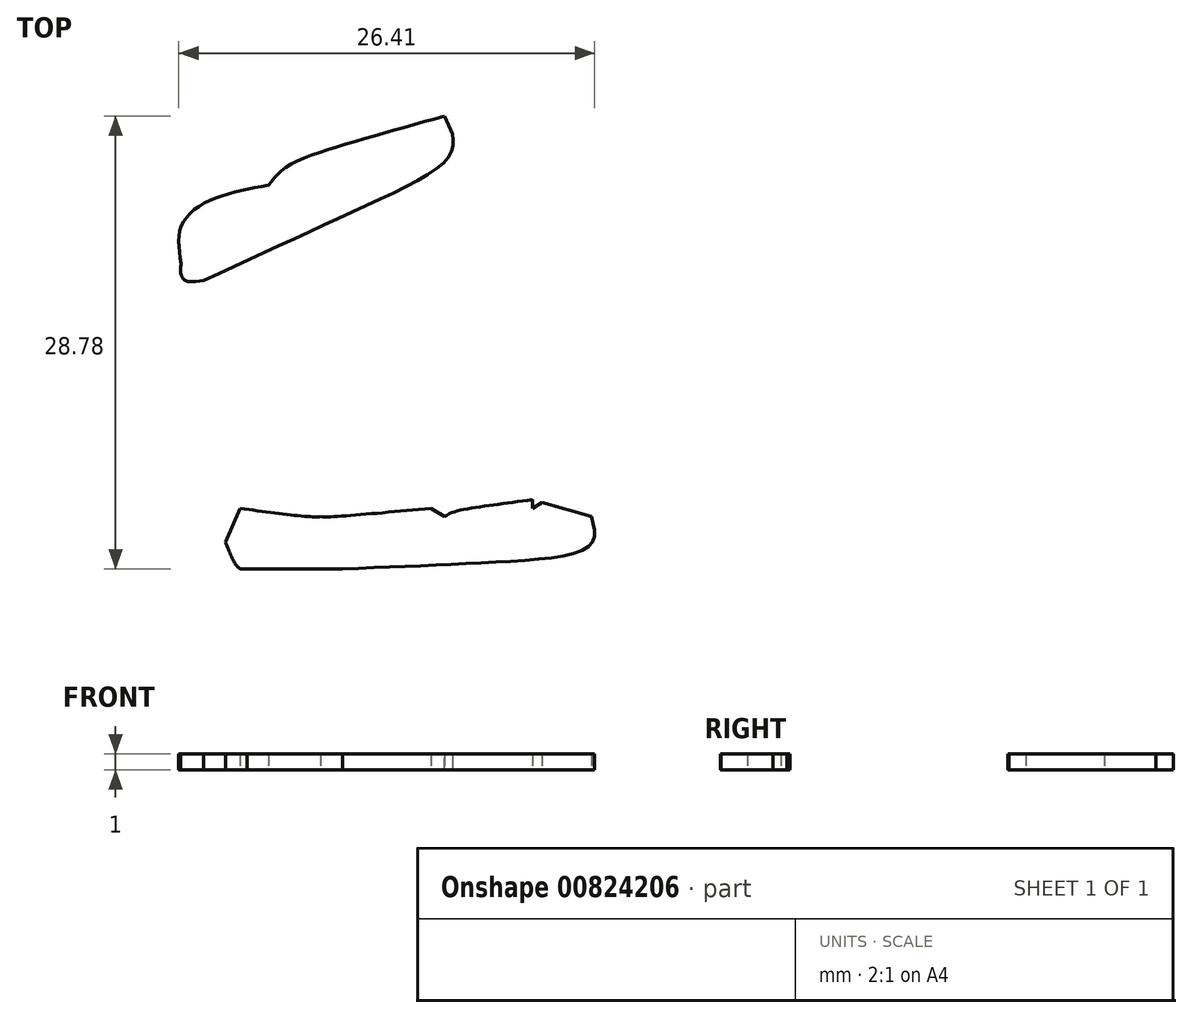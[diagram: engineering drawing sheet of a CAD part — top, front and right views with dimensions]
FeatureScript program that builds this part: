
annotation { "Feature Type Name" : "Feature", "Feature Type Description" : "" }
export const myFeature = defineFeature(function(context is Context, id is Id, definition is map)
    precondition{}
    {
        {
            var Q0;
            Q0=qCreatedBy(makeId("Top.planeOp"),FACE);
            var sketch = newSketch(context, id + "F0", { "sketchPlane" : qUnion([Q0])});
            skLineSegment(sketch, "E0", {"start": v(-130.54, 32.73) * mm, "end": v(-129.62, 32.73) * mm});
            skLineSegment(sketch, "E1", {"start": v(-129.62, 32.73) * mm, "end": v(-130.54, 32.73) * mm});
            skLineSegment(sketch, "E2", {"start": v(-121.63, 45.27) * mm, "end": v(-120.16, 45.27) * mm});
            skLineSegment(sketch, "E3", {"start": v(-120.16, 45.27) * mm, "end": v(-121.63, 45.27) * mm});
            skLineSegment(sketch, "E4", {"start": v(-119.52, 44.51) * mm, "end": v(-119.52, 36.1) * mm});
            skLineSegment(sketch, "E5", {"start": v(-119.52, 36.1) * mm, "end": v(-119.52, 44.51) * mm});
            skLineSegment(sketch, "E6", {"start": v(-112.28, 38.7) * mm, "end": v(-111.49, 37.23) * mm});
            skLineSegment(sketch, "E7", {"start": v(-111.49, 37.23) * mm, "end": v(-111.49, 36.47) * mm});
            skLineSegment(sketch, "E8", {"start": v(-111.49, 36.47) * mm, "end": v(-112.28, 38.7) * mm});
            skLineSegment(sketch, "E9", {"start": v(-129.26, 16.37) * mm, "end": v(-129.26, 17.5) * mm});
            skLineSegment(sketch, "E10", {"start": v(-129.26, 17.5) * mm, "end": v(-129.26, 16.37) * mm});
            skLineSegment(sketch, "E11", {"start": v(-131.13, 17.5) * mm, "end": v(-132.17, 17.5) * mm});
            skLineSegment(sketch, "E12", {"start": v(-132.17, 17.5) * mm, "end": v(-131.13, 17.5) * mm});
            skLineSegment(sketch, "E13", {"start": v(-133.76, 19.58) * mm, "end": v(-133.76, 26.11) * mm});
            skLineSegment(sketch, "E14", {"start": v(-133.76, 26.11) * mm, "end": v(-134.47, 27.77) * mm});
            skLineSegment(sketch, "E15", {"start": v(-134.47, 27.77) * mm, "end": v(-133.76, 19.58) * mm});
            skLineSegment(sketch, "E16", {"start": v(-144.82, 25.3) * mm, "end": v(-144.82, 26.58) * mm});
            skLineSegment(sketch, "E17", {"start": v(-144.82, 26.58) * mm, "end": v(-144.82, 25.3) * mm});
            skLineSegment(sketch, "E18", {"start": v(-134.32, 31.6) * mm, "end": v(-133.76, 34.91) * mm});
            skLineSegment(sketch, "E19", {"start": v(-133.76, 34.91) * mm, "end": v(-134.32, 31.6) * mm});
            skLineSegment(sketch, "E20", {"start": v(-135.79, 44.56) * mm, "end": v(-135.79, 45.27) * mm});
            skLineSegment(sketch, "E21", {"start": v(-135.79, 45.27) * mm, "end": v(-135.79, 44.56) * mm});
            skLineSegment(sketch, "E22", {"start": v(-141.2, 19.58) * mm, "end": v(-140.2, 19.58) * mm});
            skLineSegment(sketch, "E23", {"start": v(-140.2, 19.58) * mm, "end": v(-141.2, 19.58) * mm});
            skLineSegment(sketch, "E24", {"start": v(-115.06, 17.17) * mm, "end": v(-112.6, 17.17) * mm});
            skLineSegment(sketch, "E25", {"start": v(-112.6, 17.17) * mm, "end": v(-115.06, 17.17) * mm});
            skLineSegment(sketch, "E26", {"start": v(-108.46, 12.3) * mm, "end": v(-108.46, 11.21) * mm});
            skLineSegment(sketch, "E27", {"start": v(-108.46, 11.21) * mm, "end": v(-108.46, 12.3) * mm});
            skLineSegment(sketch, "E28", {"start": v(-125.53, -19.25) * mm, "end": v(-124.53, -19.25) * mm});
            skLineSegment(sketch, "E29", {"start": v(-124.53, -19.25) * mm, "end": v(-125.53, -19.25) * mm});
            skLineSegment(sketch, "E30", {"start": v(-89.89, -19.96) * mm, "end": v(-89.89, -20.58) * mm});
            skLineSegment(sketch, "E31", {"start": v(-89.89, -20.58) * mm, "end": v(-89.89, -19.96) * mm});
            skLineSegment(sketch, "E32", {"start": v(-106.55, -45.18) * mm, "end": v(-111, -45.18) * mm});
            skLineSegment(sketch, "E33", {"start": v(-111, -45.18) * mm, "end": v(-106.55, -45.18) * mm});
            skLineSegment(sketch, "E34", {"start": v(-100.63, -17.08) * mm, "end": v(-100.63, -16.5) * mm});
            skLineSegment(sketch, "E35", {"start": v(-100.63, -16.5) * mm, "end": v(-100.63, -17.08) * mm});
            skLineSegment(sketch, "E36", {"start": v(-125.92, -23.8) * mm, "end": v(-126.56, -25.26) * mm});
            skLineSegment(sketch, "E37", {"start": v(-126.56, -25.26) * mm, "end": v(-126.56, -33.59) * mm});
            skLineSegment(sketch, "E38", {"start": v(-126.56, -33.59) * mm, "end": v(-124.21, -33.59) * mm});
            skLineSegment(sketch, "E39", {"start": v(-124.21, -33.59) * mm, "end": v(-125.92, -23.8) * mm});
            skLineSegment(sketch, "E40", {"start": v(-116.42, -22.8) * mm, "end": v(-115.62, -22.8) * mm});
            skLineSegment(sketch, "E41", {"start": v(-115.62, -22.8) * mm, "end": v(-116.42, -22.8) * mm});
            skLineSegment(sketch, "E42", {"start": v(-110.45, -31.88) * mm, "end": v(-110.45, -33.4) * mm});
            skLineSegment(sketch, "E43", {"start": v(-110.45, -33.4) * mm, "end": v(-112.64, -34.39) * mm});
            skLineSegment(sketch, "E44", {"start": v(-112.64, -34.39) * mm, "end": v(-110.45, -31.88) * mm});
            skLineSegment(sketch, "E45", {"start": v(-130.26, -32.5) * mm, "end": v(-130.26, -25.26) * mm});
            skLineSegment(sketch, "E46", {"start": v(-130.26, -25.26) * mm, "end": v(-130.26, -32.5) * mm});
            skLineSegment(sketch, "E47", {"start": v(-142.07, -30.84) * mm, "end": v(-142.63, -30.84) * mm});
            skLineSegment(sketch, "E48", {"start": v(-142.63, -30.84) * mm, "end": v(-142.07, -30.84) * mm});
            skLineSegment(sketch, "E49", {"start": v(-142.07, -45.8) * mm, "end": v(-144.22, -45.8) * mm});
            skLineSegment(sketch, "E50", {"start": v(-144.22, -45.8) * mm, "end": v(-142.07, -45.8) * mm});
            skLineSegment(sketch, "E51", {"start": v(-145.33, -44.37) * mm, "end": v(-145.33, -42.67) * mm});
            skLineSegment(sketch, "E52", {"start": v(-145.33, -42.67) * mm, "end": v(-145.33, -44.37) * mm});
            skLineSegment(sketch, "E53", {"start": v(-147.4, -32.02) * mm, "end": v(-150.38, -35) * mm});
            skLineSegment(sketch, "E54", {"start": v(-150.38, -35) * mm, "end": v(-147.4, -32.02) * mm});
            skLineSegment(sketch, "E55", {"start": v(-152.85, -33.68) * mm, "end": v(-152.85, -31.36) * mm});
            skLineSegment(sketch, "E56", {"start": v(-152.85, -31.36) * mm, "end": v(-152.85, -33.68) * mm});
            skLineSegment(sketch, "E57", {"start": v(-148.32, -15.8) * mm, "end": v(-148.32, -14.47) * mm});
            skLineSegment(sketch, "E58", {"start": v(-148.32, -14.47) * mm, "end": v(-146.2, -14.47) * mm});
            skLineSegment(sketch, "E59", {"start": v(-146.2, -14.47) * mm, "end": v(-148.32, -15.8) * mm});
            skLineSegment(sketch, "E60", {"start": v(-144.06, -23.8) * mm, "end": v(-142.83, -25.26) * mm});
            skLineSegment(sketch, "E61", {"start": v(-142.83, -25.26) * mm, "end": v(-144.06, -23.8) * mm});
            skLineSegment(sketch, "E62", {"start": v(-128.27, -13.39) * mm, "end": v(-128.27, -12.82) * mm});
            skLineSegment(sketch, "E63", {"start": v(-128.27, -12.82) * mm, "end": v(-128.27, -13.39) * mm});
            skLineSegment(sketch, "E64", {"start": v(-129.66, -11.12) * mm, "end": v(-130.78, -11.12) * mm});
            skLineSegment(sketch, "E65", {"start": v(-130.78, -11.12) * mm, "end": v(-135.27, -14.71) * mm});
            skLineSegment(sketch, "E66", {"start": v(-135.27, -14.71) * mm, "end": v(-136.7, -14.71) * mm});
            skLineSegment(sketch, "E67", {"start": v(-136.7, -14.71) * mm, "end": v(-129.66, -11.12) * mm});
            skLineSegment(sketch, "E68", {"start": v(-139.29, -13.39) * mm, "end": v(-138.8, -10.4) * mm});
            skLineSegment(sketch, "E69", {"start": v(-138.8, -10.4) * mm, "end": v(-142.3, 17.03) * mm});
            skLineSegment(sketch, "E70", {"start": v(-142.3, 17.03) * mm, "end": v(-139.29, -13.39) * mm});
            skLineSegment(sketch, "E71", {"start": v(-125, 10.88) * mm, "end": v(-125, 4.64) * mm});
            skLineSegment(sketch, "E72", {"start": v(-125, 4.64) * mm, "end": v(-120.12, 4.64) * mm});
            skLineSegment(sketch, "E73", {"start": v(-120.12, 4.64) * mm, "end": v(-125, 10.88) * mm});
            skLineSegment(sketch, "E74", {"start": v(-119, 3.26) * mm, "end": v(-119, 2.84) * mm});
            skLineSegment(sketch, "E75", {"start": v(-119, 2.84) * mm, "end": v(-119, 3.26) * mm});
            skLineSegment(sketch, "E76", {"start": v(-122.03, 0.8) * mm, "end": v(-123.1, 1.47) * mm});
            skLineSegment(sketch, "E77", {"start": v(-123.1, 1.47) * mm, "end": v(-122.03, 0.8) * mm});
            skLineSegment(sketch, "E78", {"start": v(-125, 0.8) * mm, "end": v(-125, -4.35) * mm});
            skLineSegment(sketch, "E79", {"start": v(-125, -4.35) * mm, "end": v(-124.01, -4.35) * mm});
            skLineSegment(sketch, "E80", {"start": v(-124.01, -4.35) * mm, "end": v(-125, 0.8) * mm});
            skLineSegment(sketch, "E81", {"start": v(-117.61, -0.14) * mm, "end": v(-115.82, -0.14) * mm});
            skLineSegment(sketch, "E82", {"start": v(-115.82, -0.14) * mm, "end": v(-117.61, -0.14) * mm});
            skLineSegment(sketch, "E83", {"start": v(-111.68, 12.58) * mm, "end": v(-113, 13.34) * mm});
            skLineSegment(sketch, "E84", {"start": v(-113, 13.34) * mm, "end": v(-116.1, 13.34) * mm});
            skLineSegment(sketch, "E85", {"start": v(-116.1, 13.34) * mm, "end": v(-125, 10.88) * mm});
            skLineSegment(sketch, "E86", {"start": v(-125, 10.88) * mm, "end": v(-111.68, 12.58) * mm});
            skLineSegment(sketch, "E87", {"start": v(-137.1, 7.9) * mm, "end": v(-137.1, 2.7) * mm});
            skLineSegment(sketch, "E88", {"start": v(-137.1, 2.7) * mm, "end": v(-137.1, 7.9) * mm});
            skLineSegment(sketch, "E89", {"start": v(-135.63, 1.04) * mm, "end": v(-128.75, 2.98) * mm});
            skLineSegment(sketch, "E90", {"start": v(-128.75, 2.98) * mm, "end": v(-128.75, 9.18) * mm});
            skLineSegment(sketch, "E91", {"start": v(-128.75, 9.18) * mm, "end": v(-132.2, 9.18) * mm});
            skLineSegment(sketch, "E92", {"start": v(-132.2, 9.18) * mm, "end": v(-137.1, 7.9) * mm});
            skLineSegment(sketch, "E93", {"start": v(-137.1, 7.9) * mm, "end": v(-135.63, 1.04) * mm});
            skLineSegment(sketch, "E94", {"start": v(-56.32, 40.07) * mm, "end": v(-56.32, 33.44) * mm});
            skLineSegment(sketch, "E95", {"start": v(-56.32, 33.44) * mm, "end": v(-56.32, 40.07) * mm});
            skLineSegment(sketch, "E96", {"start": v(-56.84, 29.04) * mm, "end": v(-56.84, 25.12) * mm});
            skLineSegment(sketch, "E97", {"start": v(-56.84, 25.12) * mm, "end": v(-57.4, 17.5) * mm});
            skLineSegment(sketch, "E98", {"start": v(-57.4, 17.5) * mm, "end": v(-56.4, 17.5) * mm});
            skLineSegment(sketch, "E99", {"start": v(-56.4, 17.5) * mm, "end": v(-56.84, 29.04) * mm});
            skLineSegment(sketch, "E100", {"start": v(-45.98, 17.5) * mm, "end": v(-45.98, 18.69) * mm});
            skLineSegment(sketch, "E101", {"start": v(-45.98, 18.69) * mm, "end": v(-46.97, 20.53) * mm});
            skLineSegment(sketch, "E102", {"start": v(-46.97, 20.53) * mm, "end": v(-46.97, 21.48) * mm});
            skLineSegment(sketch, "E103", {"start": v(-46.97, 21.48) * mm, "end": v(-45.98, 17.5) * mm});
            skLineSegment(sketch, "E104", {"start": v(-43.87, 33.59) * mm, "end": v(-42.88, 33.59) * mm});
            skLineSegment(sketch, "E105", {"start": v(-42.88, 33.59) * mm, "end": v(-43.87, 33.59) * mm});
            skLineSegment(sketch, "E106", {"start": v(-41.76, 32.17) * mm, "end": v(-41.76, 28.62) * mm});
            skLineSegment(sketch, "E107", {"start": v(-41.76, 28.62) * mm, "end": v(-41.76, 32.17) * mm});
            skLineSegment(sketch, "E108", {"start": v(-10.94, 33.02) * mm, "end": v(-9.63, 30.94) * mm});
            skLineSegment(sketch, "E109", {"start": v(-9.63, 30.94) * mm, "end": v(-9.63, 20.39) * mm});
            skLineSegment(sketch, "E110", {"start": v(-9.63, 20.39) * mm, "end": v(-10.94, 33.02) * mm});
            skLineSegment(sketch, "E111", {"start": v(-11.14, -4.16) * mm, "end": v(-11.14, -6.53) * mm});
            skLineSegment(sketch, "E112", {"start": v(-11.14, -6.53) * mm, "end": v(-11.14, -4.16) * mm});
            skLineSegment(sketch, "E113", {"start": v(-14.32, 2.46) * mm, "end": v(-14.32, 4.73) * mm});
            skLineSegment(sketch, "E114", {"start": v(-14.32, 4.73) * mm, "end": v(-14.32, 2.46) * mm});
            skLineSegment(sketch, "E115", {"start": v(-22.67, -11.4) * mm, "end": v(-22, -13.06) * mm});
            skLineSegment(sketch, "E116", {"start": v(-22, -13.06) * mm, "end": v(-22.67, -11.4) * mm});
            skLineSegment(sketch, "E117", {"start": v(-6.96, -10.6) * mm, "end": v(-6.6, -11.4) * mm});
            skLineSegment(sketch, "E118", {"start": v(-6.6, -11.4) * mm, "end": v(-6.6, -11.92) * mm});
            skLineSegment(sketch, "E119", {"start": v(-6.6, -11.92) * mm, "end": v(-6.96, -10.6) * mm});
            skLineSegment(sketch, "E120", {"start": v(-68.73, -21.57) * mm, "end": v(-69.09, -20.77) * mm});
            skLineSegment(sketch, "E121", {"start": v(-69.09, -20.77) * mm, "end": v(-69.09, -20.39) * mm});
            skLineSegment(sketch, "E122", {"start": v(-69.09, -20.39) * mm, "end": v(-68.73, -21.57) * mm});
            skLineSegment(sketch, "E123", {"start": v(-65.98, -18.35) * mm, "end": v(-62.36, -18.35) * mm});
            skLineSegment(sketch, "E124", {"start": v(-62.36, -18.35) * mm, "end": v(-61.05, -17.55) * mm});
            skLineSegment(sketch, "E125", {"start": v(-61.05, -17.55) * mm, "end": v(-61.53, -10.12) * mm});
            skLineSegment(sketch, "E126", {"start": v(-61.53, -10.12) * mm, "end": v(-61.53, -7.14) * mm});
            skLineSegment(sketch, "E127", {"start": v(-61.53, -7.14) * mm, "end": v(-65.98, -18.35) * mm});
            skLineSegment(sketch, "E128", {"start": v(-61.01, -4.73) * mm, "end": v(-61.49, -3.55) * mm});
            skLineSegment(sketch, "E129", {"start": v(-61.49, -3.55) * mm, "end": v(-61.05, -2.46) * mm});
            skLineSegment(sketch, "E130", {"start": v(-61.05, -2.46) * mm, "end": v(-61.01, -4.73) * mm});
            skLineSegment(sketch, "E131", {"start": v(-60.54, 23.94) * mm, "end": v(-60.54, 25.02) * mm});
            skLineSegment(sketch, "E132", {"start": v(-60.54, 25.02) * mm, "end": v(-59.94, 26.5) * mm});
            skLineSegment(sketch, "E133", {"start": v(-59.94, 26.5) * mm, "end": v(-61.37, 27.39) * mm});
            skLineSegment(sketch, "E134", {"start": v(-61.37, 27.39) * mm, "end": v(-60.54, 23.94) * mm});
            skLineSegment(sketch, "E135", {"start": v(-67.58, 27.39) * mm, "end": v(-67.58, 28.71) * mm});
            skLineSegment(sketch, "E136", {"start": v(-67.58, 28.71) * mm, "end": v(-67.58, 27.39) * mm});
            skLineSegment(sketch, "E137", {"start": v(-59.54, 31.27) * mm, "end": v(-59.54, 40.63) * mm});
            skLineSegment(sketch, "E138", {"start": v(-59.54, 40.63) * mm, "end": v(-59.54, 31.27) * mm});
            skLineSegment(sketch, "E139", {"start": v(-42.28, 21.05) * mm, "end": v(-41.28, 21.05) * mm});
            skLineSegment(sketch, "E140", {"start": v(-41.28, 21.05) * mm, "end": v(-42.28, 21.05) * mm});
            skLineSegment(sketch, "E141", {"start": v(-36.83, 22.28) * mm, "end": v(-31.82, 22.28) * mm});
            skLineSegment(sketch, "E142", {"start": v(-31.82, 22.28) * mm, "end": v(-36.83, 22.28) * mm});
            skLineSegment(sketch, "E143", {"start": v(-30.7, 20.86) * mm, "end": v(-30.7, 20.1) * mm});
            skLineSegment(sketch, "E144", {"start": v(-30.7, 20.1) * mm, "end": v(-32.81, 19.06) * mm});
            skLineSegment(sketch, "E145", {"start": v(-32.81, 19.06) * mm, "end": v(-33.77, 19.68) * mm});
            skLineSegment(sketch, "E146", {"start": v(-33.77, 19.68) * mm, "end": v(-30.7, 20.86) * mm});
            skLineSegment(sketch, "E147", {"start": v(-43.27, 17.22) * mm, "end": v(-43.27, 9.8) * mm});
            skLineSegment(sketch, "E148", {"start": v(-43.27, 9.8) * mm, "end": v(-43.27, 17.22) * mm});
            skLineSegment(sketch, "E149", {"start": v(-37.94, 15.7) * mm, "end": v(-37.39, 15.37) * mm});
            skLineSegment(sketch, "E150", {"start": v(-37.39, 15.37) * mm, "end": v(-37.75, 14.47) * mm});
            skLineSegment(sketch, "E151", {"start": v(-37.75, 14.47) * mm, "end": v(-37.75, 13.3) * mm});
            skLineSegment(sketch, "E152", {"start": v(-37.75, 13.3) * mm, "end": v(-32.3, 13.3) * mm});
            skLineSegment(sketch, "E153", {"start": v(-32.3, 13.3) * mm, "end": v(-37.94, 15.7) * mm});
            skLineSegment(sketch, "E154", {"start": v(-38.34, -5.44) * mm, "end": v(-38.86, -5.44) * mm});
            skLineSegment(sketch, "E155", {"start": v(-38.86, -5.44) * mm, "end": v(-38.34, -5.44) * mm});
            skLineSegment(sketch, "E156", {"start": v(-43.75, 9.8) * mm, "end": v(-43.75, -5.91) * mm});
            skLineSegment(sketch, "E157", {"start": v(-43.75, -5.91) * mm, "end": v(-43.75, 9.8) * mm});
            skLineSegment(sketch, "E158", {"start": v(-45.5, -7.85) * mm, "end": v(-45.9, -7.85) * mm});
            skLineSegment(sketch, "E159", {"start": v(-45.9, -7.85) * mm, "end": v(-45.5, -7.85) * mm});
            skLineSegment(sketch, "E160", {"start": v(-48.05, 4.68) * mm, "end": v(-49.52, 4.68) * mm});
            skLineSegment(sketch, "E161", {"start": v(-49.52, 4.68) * mm, "end": v(-48.05, 4.68) * mm});
            skLineSegment(sketch, "E162", {"start": v(-57.83, -17.17) * mm, "end": v(-48.4, -17.17) * mm});
            skLineSegment(sketch, "E163", {"start": v(-48.4, -17.17) * mm, "end": v(-57.83, -17.17) * mm});
            skLineSegment(sketch, "E164", {"start": v(-27.4, -13.06) * mm, "end": v(-27.88, -9.04) * mm});
            skLineSegment(sketch, "E165", {"start": v(-27.88, -9.04) * mm, "end": v(-27.4, -13.06) * mm});
            skLineSegment(sketch, "E166", {"start": v(-42.28, 24.22) * mm, "end": v(-42.28, 21.05) * mm});
            skLineSegment(sketch, "E167", {"start": v(-42.28, 21.05) * mm, "end": v(-42.28, 24.22) * mm});
            skLineSegment(sketch, "E168", {"start": v(-20.68, 29.14) * mm, "end": v(-20.68, 17.55) * mm});
            skLineSegment(sketch, "E169", {"start": v(-20.68, 17.55) * mm, "end": v(-16.78, 16.89) * mm});
            skLineSegment(sketch, "E170", {"start": v(-16.78, 16.89) * mm, "end": v(-12.89, 16.89) * mm});
            skLineSegment(sketch, "E171", {"start": v(-12.89, 16.89) * mm, "end": v(-20.68, 29.14) * mm});
            skLineSegment(sketch, "E172", {"start": v(-57.83, 4.92) * mm, "end": v(-56.92, 4.92) * mm});
            skLineSegment(sketch, "E173", {"start": v(-56.92, 4.92) * mm, "end": v(-57.83, 4.92) * mm});
            skLineSegment(sketch, "E174", {"start": v(-46.97, 9.56) * mm, "end": v(-46.42, 16.13) * mm});
            skLineSegment(sketch, "E175", {"start": v(-46.42, 16.13) * mm, "end": v(-46.97, 9.56) * mm});
            skLineSegment(sketch, "E176", {"start": v(-57.83, 10.22) * mm, "end": v(-57.83, 4.92) * mm});
            skLineSegment(sketch, "E177", {"start": v(-57.83, 4.92) * mm, "end": v(-57.83, 10.22) * mm});
            skLineSegment(sketch, "E178", {"start": v(-21.16, 11.4) * mm, "end": v(-21.16, 7.33) * mm});
            skLineSegment(sketch, "E179", {"start": v(-21.16, 7.33) * mm, "end": v(-21.16, 11.4) * mm});
            skLineSegment(sketch, "E180", {"start": v(-17.82, 6.72) * mm, "end": v(-16.67, 7.33) * mm});
            skLineSegment(sketch, "E181", {"start": v(-16.67, 7.33) * mm, "end": v(-13.84, 7.33) * mm});
            skLineSegment(sketch, "E182", {"start": v(-13.84, 7.33) * mm, "end": v(-17.82, 6.72) * mm});
            skLineSegment(sketch, "E183", {"start": v(-13.32, 14.38) * mm, "end": v(-16.27, 13.62) * mm});
            skLineSegment(sketch, "E184", {"start": v(-16.27, 13.62) * mm, "end": v(-16.74, 13.62) * mm});
            skLineSegment(sketch, "E185", {"start": v(-16.74, 13.62) * mm, "end": v(-13.32, 14.38) * mm});
            skLineSegment(sketch, "E186", {"start": v(-36.11, 1.99) * mm, "end": v(-32.42, 8.23) * mm});
            skLineSegment(sketch, "E187", {"start": v(-32.42, 8.23) * mm, "end": v(-32.42, 10.08) * mm});
            skLineSegment(sketch, "E188", {"start": v(-32.42, 10.08) * mm, "end": v(-33.8, 10.08) * mm});
            skLineSegment(sketch, "E189", {"start": v(-33.8, 10.08) * mm, "end": v(-36.11, 1.99) * mm});
            skLineSegment(sketch, "E190", {"start": v(-49.32, -23.75) * mm, "end": v(-47.89, -23.75) * mm});
            skLineSegment(sketch, "E191", {"start": v(-47.89, -23.75) * mm, "end": v(-49.32, -23.75) * mm});
            skLineSegment(sketch, "E192", {"start": v(-46.77, -25.17) * mm, "end": v(-46.77, -25.4) * mm});
            skLineSegment(sketch, "E193", {"start": v(-46.77, -25.4) * mm, "end": v(-46.77, -25.17) * mm});
            skLineSegment(sketch, "E194", {"start": v(-55.17, -41.3) * mm, "end": v(-55.52, -40.5) * mm});
            skLineSegment(sketch, "E195", {"start": v(-55.52, -40.5) * mm, "end": v(-55.52, -38.79) * mm});
            skLineSegment(sketch, "E196", {"start": v(-55.52, -38.79) * mm, "end": v(-55.17, -41.3) * mm});
            skLineSegment(sketch, "E197", {"start": v(-50.11, -24.22) * mm, "end": v(-49.32, -23.75) * mm});
            skLineSegment(sketch, "E198", {"start": v(-49.32, -23.75) * mm, "end": v(-50.11, -24.22) * mm});
            skLineSegment(sketch, "E199", {"start": v(-22.75, -23.75) * mm, "end": v(-21.92, -23.75) * mm});
            skLineSegment(sketch, "E200", {"start": v(-21.92, -23.75) * mm, "end": v(-22.75, -23.75) * mm});
            skLineSegment(sketch, "E201", {"start": v(27.2, 29.33) * mm, "end": v(28.6, 29.33) * mm});
            skLineSegment(sketch, "E202", {"start": v(28.6, 29.33) * mm, "end": v(27.2, 29.33) * mm});
            skLineSegment(sketch, "E203", {"start": v(57.91, 38.7) * mm, "end": v(57.91, 38.17) * mm});
            skLineSegment(sketch, "E204", {"start": v(57.91, 38.17) * mm, "end": v(58.83, 38.7) * mm});
            skLineSegment(sketch, "E205", {"start": v(58.83, 38.7) * mm, "end": v(57.91, 38.7) * mm});
            skLineSegment(sketch, "E206", {"start": v(71.4, -14.38) * mm, "end": v(71.87, -15.47) * mm});
            skLineSegment(sketch, "E207", {"start": v(71.87, -15.47) * mm, "end": v(71.4, -16.6) * mm});
            skLineSegment(sketch, "E208", {"start": v(71.4, -16.6) * mm, "end": v(71.4, -14.38) * mm});
            skLineSegment(sketch, "E209", {"start": v(67.22, -38.17) * mm, "end": v(65.79, -38.17) * mm});
            skLineSegment(sketch, "E210", {"start": v(65.79, -38.17) * mm, "end": v(67.22, -38.17) * mm});
            skLineSegment(sketch, "E211", {"start": v(63, -36) * mm, "end": v(63, -34.82) * mm});
            skLineSegment(sketch, "E212", {"start": v(63, -34.82) * mm, "end": v(63, -36) * mm});
            skLineSegment(sketch, "E213", {"start": v(59.78, 34.91) * mm, "end": v(56.96, 34.91) * mm});
            skLineSegment(sketch, "E214", {"start": v(56.96, 34.91) * mm, "end": v(56.96, 34.34) * mm});
            skLineSegment(sketch, "E215", {"start": v(56.96, 34.34) * mm, "end": v(59.78, 34.91) * mm});
            skLineSegment(sketch, "E216", {"start": v(63, -21.57) * mm, "end": v(63, -22.7) * mm});
            skLineSegment(sketch, "E217", {"start": v(63, -22.7) * mm, "end": v(63, -21.57) * mm});
            skLineSegment(sketch, "E218", {"start": v(54.21, -3.36) * mm, "end": v(53.26, -3.36) * mm});
            skLineSegment(sketch, "E219", {"start": v(53.26, -3.36) * mm, "end": v(49.04, -16.6) * mm});
            skLineSegment(sketch, "E220", {"start": v(49.04, -16.6) * mm, "end": v(49.52, -19.91) * mm});
            skLineSegment(sketch, "E221", {"start": v(49.52, -19.91) * mm, "end": v(54.21, -3.36) * mm});
            skLineSegment(sketch, "E222", {"start": v(52.34, 2.22) * mm, "end": v(52.34, 3.31) * mm});
            skLineSegment(sketch, "E223", {"start": v(52.34, 3.31) * mm, "end": v(52.34, 2.22) * mm});
            skLineSegment(sketch, "E224", {"start": v(33.73, 15.47) * mm, "end": v(32.77, 17.17) * mm});
            skLineSegment(sketch, "E225", {"start": v(32.77, 17.17) * mm, "end": v(32.77, 18.83) * mm});
            skLineSegment(sketch, "E226", {"start": v(32.77, 18.83) * mm, "end": v(48.13, 25.4) * mm});
            skLineSegment(sketch, "E227", {"start": v(48.13, 25.4) * mm, "end": v(49.52, 25.4) * mm});
            skLineSegment(sketch, "E228", {"start": v(49.52, 25.4) * mm, "end": v(49.52, 31.5) * mm});
            skLineSegment(sketch, "E229", {"start": v(49.52, 31.5) * mm, "end": v(50, 32.6) * mm});
            skLineSegment(sketch, "E230", {"start": v(50, 32.6) * mm, "end": v(33.73, 15.47) * mm});
            skLineSegment(sketch, "E231", {"start": v(22.6, -5.53) * mm, "end": v(22.6, -17.12) * mm});
            skLineSegment(sketch, "E232", {"start": v(22.6, -17.12) * mm, "end": v(22.6, -5.53) * mm});
            skLineSegment(sketch, "E233", {"start": v(24.86, -23.8) * mm, "end": v(23.98, -28.24) * mm});
            skLineSegment(sketch, "E234", {"start": v(23.98, -28.24) * mm, "end": v(22.6, -28.24) * mm});
            skLineSegment(sketch, "E235", {"start": v(22.6, -28.24) * mm, "end": v(24.86, -23.8) * mm});
            skLineSegment(sketch, "E236", {"start": v(19.3, -18.3) * mm, "end": v(19.3, -13.81) * mm});
            skLineSegment(sketch, "E237", {"start": v(19.3, -13.81) * mm, "end": v(19.3, -18.3) * mm});
            skLineSegment(sketch, "E238", {"start": v(52.82, 34.25) * mm, "end": v(52.82, 33.16) * mm});
            skLineSegment(sketch, "E239", {"start": v(52.82, 33.16) * mm, "end": v(52.34, 29.9) * mm});
            skLineSegment(sketch, "E240", {"start": v(52.34, 29.9) * mm, "end": v(52.82, 34.25) * mm});
            skLineSegment(sketch, "E241", {"start": v(54.21, 32.07) * mm, "end": v(55.13, 34.86) * mm});
            skLineSegment(sketch, "E242", {"start": v(55.13, 34.86) * mm, "end": v(54.65, 34.86) * mm});
            skLineSegment(sketch, "E243", {"start": v(54.65, 34.86) * mm, "end": v(54.21, 32.07) * mm});
            skLineSegment(sketch, "E244", {"start": v(32.34, 14.9) * mm, "end": v(33.25, 14.9) * mm});
            skLineSegment(sketch, "E245", {"start": v(33.25, 14.9) * mm, "end": v(32.34, 14.9) * mm});
            skLineSegment(sketch, "E246", {"start": v(42.08, 13.25) * mm, "end": v(43.47, 11.07) * mm});
            skLineSegment(sketch, "E247", {"start": v(43.47, 11.07) * mm, "end": v(42.08, 13.25) * mm});
            skLineSegment(sketch, "E248", {"start": v(42.08, 7.71) * mm, "end": v(42.52, 6.58) * mm});
            skLineSegment(sketch, "E249", {"start": v(42.52, 6.58) * mm, "end": v(42.08, 7.71) * mm});
            skLineSegment(sketch, "E250", {"start": v(41.17, 5.53) * mm, "end": v(41.64, 1.66) * mm});
            skLineSegment(sketch, "E251", {"start": v(41.64, 1.66) * mm, "end": v(41.17, 5.53) * mm});
            skLineSegment(sketch, "E252", {"start": v(34.64, -3.36) * mm, "end": v(34.17, -3.36) * mm});
            skLineSegment(sketch, "E253", {"start": v(34.17, -3.36) * mm, "end": v(34.64, -3.36) * mm});
            skLineSegment(sketch, "E254", {"start": v(31.42, 9.46) * mm, "end": v(31.42, 13.86) * mm});
            skLineSegment(sketch, "E255", {"start": v(31.42, 13.86) * mm, "end": v(31.42, 9.46) * mm});
            skLineSegment(sketch, "E256", {"start": v(35.56, 6.58) * mm, "end": v(35.56, 3.88) * mm});
            skLineSegment(sketch, "E257", {"start": v(35.56, 3.88) * mm, "end": v(36.03, 3.88) * mm});
            skLineSegment(sketch, "E258", {"start": v(36.03, 3.88) * mm, "end": v(35.56, 6.58) * mm});
            skLineSegment(sketch, "E259", {"start": v(38.86, 8.23) * mm, "end": v(38.38, 8.23) * mm});
            skLineSegment(sketch, "E260", {"start": v(38.38, 8.23) * mm, "end": v(38.86, 8.23) * mm});
            skLineSegment(sketch, "E261", {"start": v(45.34, -3.88) * mm, "end": v(45.82, -3.88) * mm});
            skLineSegment(sketch, "E262", {"start": v(45.82, -3.88) * mm, "end": v(45.82, -5.01) * mm});
            skLineSegment(sketch, "E263", {"start": v(45.82, -5.01) * mm, "end": v(45.34, -3.88) * mm});
            skLineSegment(sketch, "E264", {"start": v(30.03, -14.33) * mm, "end": v(29.51, -14.38) * mm});
            skLineSegment(sketch, "E265", {"start": v(29.51, -14.38) * mm, "end": v(30.03, -14.33) * mm});
            skLineSegment(sketch, "E266", {"start": v(45.34, -3.88) * mm, "end": v(45.34, -3.88) * mm});
            skLineSegment(sketch, "E267", {"start": v(50.91, -28.24) * mm, "end": v(50.91, -28.8) * mm});
            skLineSegment(sketch, "E268", {"start": v(50.91, -28.8) * mm, "end": v(51.82, -28.24) * mm});
            skLineSegment(sketch, "E269", {"start": v(51.82, -28.24) * mm, "end": v(54.65, -28.24) * mm});
            skLineSegment(sketch, "E270", {"start": v(54.65, -28.24) * mm, "end": v(54.65, -29.33) * mm});
            skLineSegment(sketch, "E271", {"start": v(54.65, -29.33) * mm, "end": v(50.91, -28.24) * mm});
            skLineSegment(sketch, "E272", {"start": v(38.86, -32.64) * mm, "end": v(32.77, -32.64) * mm});
            skLineSegment(sketch, "E273", {"start": v(32.77, -32.64) * mm, "end": v(38.86, -32.64) * mm});
            skLineSegment(sketch, "E274", {"start": v(31.42, -30.94) * mm, "end": v(31.42, -30.42) * mm});
            skLineSegment(sketch, "E275", {"start": v(31.42, -30.42) * mm, "end": v(32.34, -28.8) * mm});
            skLineSegment(sketch, "E276", {"start": v(32.34, -28.8) * mm, "end": v(31.42, -30.94) * mm});
            skLineSegment(sketch, "E277", {"start": v(44.47, -28.8) * mm, "end": v(45.34, -29.33) * mm});
            skLineSegment(sketch, "E278", {"start": v(45.34, -29.33) * mm, "end": v(44.47, -28.8) * mm});
            skLineSegment(sketch, "E279", {"start": v(134.12, 43.61) * mm, "end": v(136.07, 43.61) * mm});
            skLineSegment(sketch, "E280", {"start": v(136.07, 43.61) * mm, "end": v(134.12, 43.61) * mm});
            skLineSegment(sketch, "E281", {"start": v(136.74, 30.6) * mm, "end": v(136.74, 26.77) * mm});
            skLineSegment(sketch, "E282", {"start": v(136.74, 26.77) * mm, "end": v(147.68, 26.77) * mm});
            skLineSegment(sketch, "E283", {"start": v(147.68, 26.77) * mm, "end": v(136.74, 30.6) * mm});
            skLineSegment(sketch, "E284", {"start": v(141.87, 11.35) * mm, "end": v(141.87, 10.64) * mm});
            skLineSegment(sketch, "E285", {"start": v(141.87, 10.64) * mm, "end": v(142.55, 10.64) * mm});
            skLineSegment(sketch, "E286", {"start": v(142.55, 10.64) * mm, "end": v(141.87, 11.35) * mm});
            skLineSegment(sketch, "E287", {"start": v(150.26, 9.08) * mm, "end": v(150.26, 8.33) * mm});
            skLineSegment(sketch, "E288", {"start": v(150.26, 8.33) * mm, "end": v(150.26, 9.08) * mm});
            skLineSegment(sketch, "E289", {"start": v(136.07, -36.23) * mm, "end": v(136.74, -41.63) * mm});
            skLineSegment(sketch, "E290", {"start": v(136.74, -41.63) * mm, "end": v(134.8, -43.14) * mm});
            skLineSegment(sketch, "E291", {"start": v(134.8, -43.14) * mm, "end": v(132.88, -43.14) * mm});
            skLineSegment(sketch, "E292", {"start": v(132.88, -43.14) * mm, "end": v(136.07, -36.23) * mm});
            skLineSegment(sketch, "E293", {"start": v(131.57, -41.63) * mm, "end": v(131.57, -40.87) * mm});
            skLineSegment(sketch, "E294", {"start": v(131.57, -40.87) * mm, "end": v(131.57, -41.63) * mm});
            skLineSegment(sketch, "E295", {"start": v(132.88, 4.5) * mm, "end": v(130.3, 4.5) * mm});
            skLineSegment(sketch, "E296", {"start": v(130.3, 4.5) * mm, "end": v(132.88, 4.5) * mm});
            skLineSegment(sketch, "E297", {"start": v(119.24, 3.74) * mm, "end": v(119.24, 5.25) * mm});
            skLineSegment(sketch, "E298", {"start": v(119.24, 5.25) * mm, "end": v(119.24, 3.74) * mm});
            skLineSegment(sketch, "E299", {"start": v(132.2, 8.33) * mm, "end": v(132.88, 9.89) * mm});
            skLineSegment(sketch, "E300", {"start": v(132.88, 9.89) * mm, "end": v(132.88, 10.64) * mm});
            skLineSegment(sketch, "E301", {"start": v(132.88, 10.64) * mm, "end": v(132.2, 8.33) * mm});
            skLineSegment(sketch, "E302", {"start": v(133.48, 23.7) * mm, "end": v(132.88, 23.7) * mm});
            skLineSegment(sketch, "E303", {"start": v(132.88, 23.7) * mm, "end": v(133.48, 23.7) * mm});
            skLineSegment(sketch, "E304", {"start": v(110.25, 1.42) * mm, "end": v(110.25, -1.66) * mm});
            skLineSegment(sketch, "E305", {"start": v(110.25, -1.66) * mm, "end": v(110.25, 1.42) * mm});
            skLineSegment(sketch, "E306", {"start": v(112.16, -13.95) * mm, "end": v(110.25, -15.47) * mm});
            skLineSegment(sketch, "E307", {"start": v(110.25, -15.47) * mm, "end": v(108.94, -15.47) * mm});
            skLineSegment(sketch, "E308", {"start": v(108.94, -15.47) * mm, "end": v(112.16, -13.95) * mm});
            skLineSegment(sketch, "E309", {"start": v(108.94, 36) * mm, "end": v(111.56, 36) * mm});
            skLineSegment(sketch, "E310", {"start": v(111.56, 36) * mm, "end": v(111.56, 27.58) * mm});
            skLineSegment(sketch, "E311", {"start": v(111.56, 27.58) * mm, "end": v(110.85, 19.87) * mm});
            skLineSegment(sketch, "E312", {"start": v(110.85, 19.87) * mm, "end": v(108.94, 36) * mm});
            skLineSegment(sketch, "E313", {"start": v(133.48, 26.02) * mm, "end": v(133.48, 26.77) * mm});
            skLineSegment(sketch, "E314", {"start": v(133.48, 26.77) * mm, "end": v(133.48, 26.02) * mm});
            skLineSegment(sketch, "E315", {"start": v(134.12, 41.34) * mm, "end": v(134.12, 43.61) * mm});
            skLineSegment(sketch, "E316", {"start": v(134.12, 43.61) * mm, "end": v(134.12, 41.34) * mm});
            skLineSegment(sketch, "E317", {"start": v(136.74, 24.5) * mm, "end": v(136.74, 10.64) * mm});
            skLineSegment(sketch, "E318", {"start": v(136.74, 10.64) * mm, "end": v(136.74, 24.5) * mm});
            skLineSegment(sketch, "E319", {"start": v(150.26, 21.38) * mm, "end": v(150.26, 22.94) * mm});
            skLineSegment(sketch, "E320", {"start": v(150.26, 22.94) * mm, "end": v(150.26, 21.38) * mm});
            skLineSegment(sketch, "E321", {"start": v(149, 24.5) * mm, "end": v(136.74, 24.5) * mm});
            skLineSegment(sketch, "E322", {"start": v(136.74, 24.5) * mm, "end": v(149, 24.5) * mm});
            skFitSpline(sketch, "E323", {"points": [v(-134.63, 45.8) * mm, v(-131.9, 44.53) * mm, v(-130.54, 40.18) * mm, v(-130.54, 32.73) * mm]});
            skFitSpline(sketch, "E324", {"points": [v(-129.62, 32.73) * mm, v(-125, 33.71) * mm, v(-122.7, 35.26) * mm, v(-122.7, 37.37) * mm]});
            skFitSpline(sketch, "E325", {"points": [v(-122.7, 37.37) * mm, v(-122.49, 42.64) * mm, v(-122.13, 45.27) * mm, v(-121.63, 45.27) * mm]});
            skFitSpline(sketch, "E326", {"points": [v(-120.16, 45.27) * mm, v(-119.73, 45.18) * mm, v(-119.52, 44.92) * mm, v(-119.52, 44.51) * mm]});
            skFitSpline(sketch, "E327", {"points": [v(-119.52, 36.1) * mm, v(-115.12, 37.83) * mm, v(-112.7, 38.7) * mm, v(-112.28, 38.7) * mm]});
            skFitSpline(sketch, "E328", {"points": [v(-111.49, 36.47) * mm, v(-114.14, 34.58) * mm, v(-116.93, 33.2) * mm, v(-119.88, 32.36) * mm]});
            skFitSpline(sketch, "E329", {"points": [v(-119.88, 32.36) * mm, v(-121.95, 26.08) * mm, v(-123.64, 21.84) * mm, v(-124.97, 19.63) * mm]});
            skFitSpline(sketch, "E330", {"points": [v(-124.97, 19.63) * mm, v(-125.6, 17.05) * mm, v(-126.63, 15.75) * mm, v(-128.03, 15.75) * mm]});
            skFitSpline(sketch, "E331", {"points": [v(-128.03, 15.75) * mm, v(-128.67, 16.16) * mm, v(-129.08, 16.37) * mm, v(-129.26, 16.37) * mm]});
            skFitSpline(sketch, "E332", {"points": [v(-129.26, 17.5) * mm, v(-126.7, 21.5) * mm, v(-125.15, 25.73) * mm, v(-124.65, 30.18) * mm]});
            skFitSpline(sketch, "E333", {"points": [v(-124.65, 30.18) * mm, v(-128.57, 29.58) * mm, v(-130.54, 28.59) * mm, v(-130.54, 27.2) * mm]});
            skFitSpline(sketch, "E334", {"points": [v(-130.54, 27.2) * mm, v(-130.54, 25.53) * mm, v(-130.38, 23.92) * mm, v(-130.06, 22.37) * mm]});
            skFitSpline(sketch, "E335", {"points": [v(-130.06, 22.37) * mm, v(-130.35, 19.13) * mm, v(-130.7, 17.5) * mm, v(-131.13, 17.5) * mm]});
            skFitSpline(sketch, "E336", {"points": [v(-132.17, 17.5) * mm, v(-132.54, 17.5) * mm, v(-133.07, 18.2) * mm, v(-133.76, 19.58) * mm]});
            skFitSpline(sketch, "E337", {"points": [v(-134.47, 27.77) * mm, v(-139.04, 26.13) * mm, v(-142.48, 25.3) * mm, v(-144.82, 25.3) * mm]});
            skFitSpline(sketch, "E338", {"points": [v(-144.82, 26.58) * mm, v(-144.82, 27.47) * mm, v(-141.32, 29.14) * mm, v(-134.32, 31.6) * mm]});
            skFitSpline(sketch, "E339", {"points": [v(-133.76, 34.91) * mm, v(-133.76, 35.6) * mm, v(-134.43, 38.82) * mm, v(-135.79, 44.56) * mm]});
            skFitSpline(sketch, "E340", {"points": [v(-135.79, 45.27) * mm, v(-135.63, 45.27) * mm, v(-135.24, 45.44) * mm, v(-134.63, 45.8) * mm]});
            skFitSpline(sketch, "E341", {"points": [v(-140.2, 19.58) * mm, v(-139.43, 19.58) * mm, v(-138.7, 17) * mm, v(-138.01, 11.83) * mm]});
            skFitSpline(sketch, "E342", {"points": [v(-138.01, 11.83) * mm, v(-136.4, 11.83) * mm, v(-128.75, 13.6) * mm, v(-115.06, 17.17) * mm]});
            skFitSpline(sketch, "E343", {"points": [v(-112.6, 17.17) * mm, v(-109.84, 16.7) * mm, v(-108.46, 15.07) * mm, v(-108.46, 12.3) * mm]});
            skFitSpline(sketch, "E344", {"points": [v(-108.46, 11.21) * mm, v(-112.17, -1.4) * mm, v(-116.59, -9.05) * mm, v(-121.7, -11.73) * mm]});
            skFitSpline(sketch, "E345", {"points": [v(-121.7, -11.73) * mm, v(-124.25, -11.73) * mm, v(-125.53, -14.24) * mm, v(-125.53, -19.25) * mm]});
            skFitSpline(sketch, "E346", {"points": [v(-124.53, -19.25) * mm, v(-113.69, -15.28) * mm, v(-105.7, -13.3) * mm, v(-100.55, -13.3) * mm]});
            skFitSpline(sketch, "E347", {"points": [v(-100.55, -13.3) * mm, v(-100.23, -13.3) * mm, v(-99.71, -13.5) * mm, v(-99, -13.9) * mm]});
            skFitSpline(sketch, "E348", {"points": [v(-99, -13.9) * mm, v(-98.3, -13.5) * mm, v(-97.83, -13.3) * mm, v(-97.56, -13.3) * mm]});
            skFitSpline(sketch, "E349", {"points": [v(-97.56, -13.3) * mm, v(-92.45, -14.27) * mm, v(-89.89, -16.5) * mm, v(-89.89, -19.96) * mm]});
            skFitSpline(sketch, "E350", {"points": [v(-89.89, -20.58) * mm, v(-89.89, -27.96) * mm, v(-94, -35.78) * mm, v(-102.22, -44.04) * mm]});
            skFitSpline(sketch, "E351", {"points": [v(-102.22, -44.04) * mm, v(-104.29, -44.8) * mm, v(-105.73, -45.18) * mm, v(-106.55, -45.18) * mm]});
            skFitSpline(sketch, "E352", {"points": [v(-111, -45.18) * mm, v(-114.22, -43.7) * mm, v(-115.94, -42.45) * mm, v(-116.18, -41.44) * mm]});
            skFitSpline(sketch, "E353", {"points": [v(-116.18, -41.44) * mm, v(-116.18, -40.74) * mm, v(-115.67, -40.3) * mm, v(-114.67, -40.11) * mm]});
            skFitSpline(sketch, "E354", {"points": [v(-114.67, -40.11) * mm, v(-113.05, -41.34) * mm, v(-110.85, -41.96) * mm, v(-108.06, -41.96) * mm]});
            skFitSpline(sketch, "E355", {"points": [v(-108.06, -41.96) * mm, v(-102.52, -41.96) * mm, v(-97.37, -35.24) * mm, v(-92.6, -21.8) * mm]});
            skFitSpline(sketch, "E356", {"points": [v(-92.6, -21.8) * mm, v(-92.6, -18.97) * mm, v(-94.93, -17.2) * mm, v(-99.6, -16.5) * mm]});
            skFitSpline(sketch, "E357", {"points": [v(-99.6, -16.5) * mm, v(-100.26, -16.89) * mm, v(-100.6, -17.08) * mm, v(-100.63, -17.08) * mm]});
            skFitSpline(sketch, "E358", {"points": [v(-100.63, -16.5) * mm, v(-104.07, -16.5) * mm, v(-112.5, -18.94) * mm, v(-125.92, -23.8) * mm]});
            skFitSpline(sketch, "E359", {"points": [v(-124.21, -33.59) * mm, v(-124.21, -32.83) * mm, v(-121.61, -29.23) * mm, v(-116.42, -22.8) * mm]});
            skFitSpline(sketch, "E360", {"points": [v(-115.62, -22.8) * mm, v(-115.22, -22.8) * mm, v(-114.48, -25.15) * mm, v(-113.4, -29.85) * mm]});
            skFitSpline(sketch, "E361", {"points": [v(-113.4, -29.85) * mm, v(-111.43, -30.89) * mm, v(-110.45, -31.57) * mm, v(-110.45, -31.88) * mm]});
            skFitSpline(sketch, "E362", {"points": [v(-112.64, -34.39) * mm, v(-113.86, -34.39) * mm, v(-115.52, -32.92) * mm, v(-117.61, -30) * mm]});
            skFitSpline(sketch, "E363", {"points": [v(-117.61, -30) * mm, v(-121.59, -35.32) * mm, v(-124.73, -37.99) * mm, v(-127.04, -37.99) * mm]});
            skFitSpline(sketch, "E364", {"points": [v(-127.04, -37.99) * mm, v(-129.18, -36.91) * mm, v(-130.26, -35.08) * mm, v(-130.26, -32.5) * mm]});
            skFitSpline(sketch, "E365", {"points": [v(-130.26, -25.26) * mm, v(-138.13, -28.57) * mm, v(-142.07, -30.43) * mm, v(-142.07, -30.84) * mm]});
            skFitSpline(sketch, "E366", {"points": [v(-142.63, -30.84) * mm, v(-141.94, -38.22) * mm, v(-141.6, -42.73) * mm, v(-141.6, -44.37) * mm]});
            skFitSpline(sketch, "E367", {"points": [v(-141.6, -44.37) * mm, v(-141.91, -45.13) * mm, v(-142.07, -45.6) * mm, v(-142.07, -45.8) * mm]});
            skFitSpline(sketch, "E368", {"points": [v(-144.22, -45.8) * mm, v(-144.54, -45.8) * mm, v(-144.9, -45.32) * mm, v(-145.33, -44.37) * mm]});
            skFitSpline(sketch, "E369", {"points": [v(-145.33, -42.67) * mm, v(-145.33, -42.57) * mm, v(-145.15, -42.53) * mm, v(-144.78, -42.53) * mm]});
            skFitSpline(sketch, "E370", {"points": [v(-144.78, -42.53) * mm, v(-145.5, -35.53) * mm, v(-146.37, -32.02) * mm, v(-147.4, -32.02) * mm]});
            skFitSpline(sketch, "E371", {"points": [v(-150.38, -35) * mm, v(-151.82, -35) * mm, v(-152.64, -34.56) * mm, v(-152.85, -33.68) * mm]});
            skFitSpline(sketch, "E372", {"points": [v(-152.85, -31.36) * mm, v(-152.64, -30.23) * mm, v(-150.6, -28.92) * mm, v(-146.76, -27.44) * mm]});
            skFitSpline(sketch, "E373", {"points": [v(-146.76, -27.44) * mm, v(-147.8, -22.42) * mm, v(-148.32, -18.54) * mm, v(-148.32, -15.8) * mm]});
            skFitSpline(sketch, "E374", {"points": [v(-146.2, -14.47) * mm, v(-145.76, -14.47) * mm, v(-145.04, -17.58) * mm, v(-144.06, -23.8) * mm]});
            skFitSpline(sketch, "E375", {"points": [v(-142.83, -25.26) * mm, v(-133.44, -23.24) * mm, v(-128.75, -21.1) * mm, v(-128.75, -18.83) * mm]});
            skFitSpline(sketch, "E376", {"points": [v(-128.75, -18.83) * mm, v(-128.43, -16.68) * mm, v(-128.27, -14.87) * mm, v(-128.27, -13.39) * mm]});
            skFitSpline(sketch, "E377", {"points": [v(-128.27, -12.82) * mm, v(-128.27, -11.68) * mm, v(-128.73, -11.12) * mm, v(-129.66, -11.12) * mm]});
            skFitSpline(sketch, "E378", {"points": [v(-136.7, -14.71) * mm, v(-138.21, -14.71) * mm, v(-139.07, -14.27) * mm, v(-139.29, -13.39) * mm]});
            skFitSpline(sketch, "E379", {"points": [v(-142.3, 17.03) * mm, v(-141.94, 18.73) * mm, v(-141.57, 19.58) * mm, v(-141.2, 19.58) * mm]});
            skFitSpline(sketch, "E380", {"points": [v(-120.12, 4.64) * mm, v(-119.77, 4.64) * mm, v(-119.4, 4.18) * mm, v(-119, 3.26) * mm]});
            skFitSpline(sketch, "E381", {"points": [v(-119, 2.84) * mm, v(-119.45, 1.48) * mm, v(-120.46, 0.8) * mm, v(-122.03, 0.8) * mm]});
            skFitSpline(sketch, "E382", {"points": [v(-123.1, 1.47) * mm, v(-123.82, 1.02) * mm, v(-124.45, 0.8) * mm, v(-125, 0.8) * mm]});
            skFitSpline(sketch, "E383", {"points": [v(-124.01, -4.35) * mm, v(-120.22, -1.55) * mm, v(-118.09, -0.14) * mm, v(-117.61, -0.14) * mm]});
            skFitSpline(sketch, "E384", {"points": [v(-115.82, -0.14) * mm, v(-113.06, 6.67) * mm, v(-111.68, 10.91) * mm, v(-111.68, 12.58) * mm]});
            skFitSpline(sketch, "E385", {"points": [v(-137.1, 2.7) * mm, v(-136.91, 1.6) * mm, v(-136.42, 1.04) * mm, v(-135.63, 1.04) * mm]});
            skFitSpline(sketch, "E386", {"points": [v(-136.1, -3.55) * mm, v(-135.57, -7.24) * mm, v(-134.91, -9.08) * mm, v(-134.12, -9.08) * mm]});
            skFitSpline(sketch, "E387", {"points": [v(-134.12, -9.08) * mm, v(-131.3, -8.3) * mm, v(-129.32, -7.16) * mm, v(-128.15, -5.68) * mm]});
            skFitSpline(sketch, "E388", {"points": [v(-128.15, -5.68) * mm, v(-128.55, -4.95) * mm, v(-128.75, -3.58) * mm, v(-128.75, -1.56) * mm]});
            skFitSpline(sketch, "E389", {"points": [v(-128.75, -1.56) * mm, v(-129.86, -1.56) * mm, v(-132.31, -2.22) * mm, v(-136.1, -3.55) * mm]});
            skFitSpline(sketch, "E390", {"points": [v(-58.98, 41.4) * mm, v(-57.2, 41.17) * mm, v(-56.32, 40.73) * mm, v(-56.32, 40.07) * mm]});
            skFitSpline(sketch, "E391", {"points": [v(-56.32, 33.44) * mm, v(-51.55, 35.15) * mm, v(-48.42, 36) * mm, v(-46.93, 36) * mm]});
            skFitSpline(sketch, "E392", {"points": [v(-46.93, 36) * mm, v(-45.82, 35.5) * mm, v(-45.26, 35.05) * mm, v(-45.26, 34.67) * mm]});
            skFitSpline(sketch, "E393", {"points": [v(-45.26, 34.67) * mm, v(-45.26, 34.42) * mm, v(-49.12, 32.55) * mm, v(-56.84, 29.04) * mm]});
            skFitSpline(sketch, "E394", {"points": [v(-56.4, 17.5) * mm, v(-51.79, 18.3) * mm, v(-49.32, 18.69) * mm, v(-49, 18.69) * mm]});
            skFitSpline(sketch, "E395", {"points": [v(-49, 18.69) * mm, v(-47.91, 17.9) * mm, v(-46.9, 17.5) * mm, v(-45.98, 17.5) * mm]});
            skFitSpline(sketch, "E396", {"points": [v(-46.97, 21.48) * mm, v(-45.12, 29.55) * mm, v(-44.08, 33.59) * mm, v(-43.87, 33.59) * mm]});
            skFitSpline(sketch, "E397", {"points": [v(-42.88, 33.59) * mm, v(-42.56, 33.59) * mm, v(-42.19, 33.11) * mm, v(-41.76, 32.17) * mm]});
            skFitSpline(sketch, "E398", {"points": [v(-41.76, 28.62) * mm, v(-34.2, 32.34) * mm, v(-29.05, 34.2) * mm, v(-26.3, 34.2) * mm]});
            skFitSpline(sketch, "E399", {"points": [v(-26.3, 34.2) * mm, v(-25.12, 34.2) * mm, v(-23.47, 33.18) * mm, v(-21.32, 31.13) * mm]});
            skFitSpline(sketch, "E400", {"points": [v(-21.32, 31.13) * mm, v(-19.67, 32.39) * mm, v(-16.21, 33.02) * mm, v(-10.94, 33.02) * mm]});
            skFitSpline(sketch, "E401", {"points": [v(-9.63, 20.39) * mm, v(-9.63, 20.3) * mm, v(-9.78, 20.25) * mm, v(-10.1, 20.25) * mm]});
            skFitSpline(sketch, "E402", {"points": [v(-10.1, 20.25) * mm, v(-10.1, 19.2) * mm, v(-9.97, 18.69) * mm, v(-9.7, 18.69) * mm]});
            skFitSpline(sketch, "E403", {"points": [v(-9.7, 18.69) * mm, v(-10.66, 13.48) * mm, v(-11.14, 5.87) * mm, v(-11.14, -4.16) * mm]});
            skFitSpline(sketch, "E404", {"points": [v(-11.14, -6.53) * mm, v(-11.14, -6.9) * mm, v(-11.67, -7.33) * mm, v(-12.73, -7.8) * mm]});
            skFitSpline(sketch, "E405", {"points": [v(-12.73, -7.8) * mm, v(-14.48, -7.2) * mm, v(-15.35, -5.03) * mm, v(-15.35, -1.28) * mm]});
            skFitSpline(sketch, "E406", {"points": [v(-15.35, -1.28) * mm, v(-14.66, 0.02) * mm, v(-14.32, 1.26) * mm, v(-14.32, 2.46) * mm]});
            skFitSpline(sketch, "E407", {"points": [v(-14.32, 4.73) * mm, v(-19.22, 4.1) * mm, v(-21.68, 2.95) * mm, v(-21.68, 1.28) * mm]});
            skFitSpline(sketch, "E408", {"points": [v(-21.68, 1.28) * mm, v(-22.34, -3.7) * mm, v(-22.67, -7.93) * mm, v(-22.67, -11.4) * mm]});
            skFitSpline(sketch, "E409", {"points": [v(-22, -13.06) * mm, v(-14.94, -11.42) * mm, v(-9.93, -10.6) * mm, v(-6.96, -10.6) * mm]});
            skFitSpline(sketch, "E410", {"points": [v(-6.6, -11.92) * mm, v(-6.6, -14.16) * mm, v(-8.15, -15.78) * mm, v(-11.26, -16.8) * mm]});
            skFitSpline(sketch, "E411", {"points": [v(-11.26, -16.8) * mm, v(-12.02, -16.8) * mm, v(-13.85, -16.4) * mm, v(-16.74, -15.61) * mm]});
            skFitSpline(sketch, "E412", {"points": [v(-16.74, -15.61) * mm, v(-33.98, -19.58) * mm, v(-51.3, -21.57) * mm, v(-68.73, -21.57) * mm]});
            skFitSpline(sketch, "E413", {"points": [v(-69.09, -20.39) * mm, v(-68.6, -19.03) * mm, v(-67.58, -18.35) * mm, v(-65.98, -18.35) * mm]});
            skFitSpline(sketch, "E414", {"points": [v(-61.53, -7.14) * mm, v(-61.53, -6.32) * mm, v(-61.36, -5.52) * mm, v(-61.01, -4.73) * mm]});
            skFitSpline(sketch, "E415", {"points": [v(-61.05, -2.46) * mm, v(-61.05, -1.9) * mm, v(-61.21, -1.21) * mm, v(-61.53, -0.43) * mm]});
            skFitSpline(sketch, "E416", {"points": [v(-61.53, -0.43) * mm, v(-60.87, 7.02) * mm, v(-60.54, 15.14) * mm, v(-60.54, 23.94) * mm]});
            skFitSpline(sketch, "E417", {"points": [v(-61.37, 27.39) * mm, v(-61.87, 27.39) * mm, v(-63.54, 27.18) * mm, v(-66.38, 26.77) * mm]});
            skFitSpline(sketch, "E418", {"points": [v(-66.38, 26.77) * mm, v(-67.04, 27.18) * mm, v(-67.44, 27.39) * mm, v(-67.58, 27.39) * mm]});
            skFitSpline(sketch, "E419", {"points": [v(-67.58, 28.71) * mm, v(-67.58, 29.5) * mm, v(-64.9, 30.35) * mm, v(-59.54, 31.27) * mm]});
            skFitSpline(sketch, "E420", {"points": [v(-59.54, 40.63) * mm, v(-59.46, 41.14) * mm, v(-59.28, 41.4) * mm, v(-58.98, 41.4) * mm]});
            skFitSpline(sketch, "E421", {"points": [v(-41.28, 21.05) * mm, v(-39.11, 21.87) * mm, v(-37.63, 22.28) * mm, v(-36.83, 22.28) * mm]});
            skFitSpline(sketch, "E422", {"points": [v(-31.82, 22.28) * mm, v(-31.5, 22.28) * mm, v(-31.13, 21.8) * mm, v(-30.7, 20.86) * mm]});
            skFitSpline(sketch, "E423", {"points": [v(-33.77, 19.68) * mm, v(-39.23, 18.04) * mm, v(-42.4, 17.22) * mm, v(-43.27, 17.22) * mm]});
            skFitSpline(sketch, "E424", {"points": [v(-43.27, 9.8) * mm, v(-41.15, 13.73) * mm, v(-39.38, 15.7) * mm, v(-37.94, 15.7) * mm]});
            skFitSpline(sketch, "E425", {"points": [v(-32.3, 13.3) * mm, v(-29.9, 13.04) * mm, v(-28.72, 11.83) * mm, v(-28.72, 9.65) * mm]});
            skFitSpline(sketch, "E426", {"points": [v(-28.72, 9.65) * mm, v(-30.5, 2.37) * mm, v(-33.16, -1.28) * mm, v(-36.71, -1.28) * mm]});
            skFitSpline(sketch, "E427", {"points": [v(-36.71, -1.28) * mm, v(-36.71, -4.05) * mm, v(-37.25, -5.44) * mm, v(-38.34, -5.44) * mm]});
            skFitSpline(sketch, "E428", {"points": [v(-38.86, -5.44) * mm, v(-39.7, -5.44) * mm, v(-40.6, -0.68) * mm, v(-41.52, 8.85) * mm]});
            skFitSpline(sketch, "E429", {"points": [v(-41.52, 8.85) * mm, v(-42.03, 8.85) * mm, v(-42.77, 9.16) * mm, v(-43.75, 9.8) * mm]});
            skFitSpline(sketch, "E430", {"points": [v(-43.75, -5.91) * mm, v(-43.75, -6.35) * mm, v(-44.33, -7) * mm, v(-45.5, -7.85) * mm]});
            skFitSpline(sketch, "E431", {"points": [v(-45.9, -7.85) * mm, v(-46.59, -7.85) * mm, v(-47.3, -3.67) * mm, v(-48.05, 4.68) * mm]});
            skFitSpline(sketch, "E432", {"points": [v(-49.52, 4.68) * mm, v(-50.45, 3.86) * mm, v(-52.13, 3.06) * mm, v(-54.57, 2.27) * mm]});
            skFitSpline(sketch, "E433", {"points": [v(-54.57, 2.27) * mm, v(-56.5, 0.82) * mm, v(-57.76, -0.73) * mm, v(-58.35, -2.37) * mm]});
            skFitSpline(sketch, "E434", {"points": [v(-58.35, -2.37) * mm, v(-57.68, -4.54) * mm, v(-57.35, -7.3) * mm, v(-57.35, -10.64) * mm]});
            skFitSpline(sketch, "E435", {"points": [v(-57.35, -10.64) * mm, v(-57.67, -14.14) * mm, v(-57.83, -16.32) * mm, v(-57.83, -17.17) * mm]});
            skFitSpline(sketch, "E436", {"points": [v(-48.4, -17.17) * mm, v(-34.4, -16.07) * mm, v(-27.4, -14.7) * mm, v(-27.4, -13.06) * mm]});
            skFitSpline(sketch, "E437", {"points": [v(-27.88, -9.04) * mm, v(-27.03, -7.68) * mm, v(-26.21, -7) * mm, v(-25.42, -7) * mm]});
            skFitSpline(sketch, "E438", {"points": [v(-25.42, -7) * mm, v(-24.06, 10.19) * mm, v(-23.39, 21.29) * mm, v(-23.39, 26.3) * mm]});
            skFitSpline(sketch, "E439", {"points": [v(-23.39, 26.3) * mm, v(-23.39, 28) * mm, v(-24.31, 29.77) * mm, v(-26.17, 31.6) * mm]});
            skFitSpline(sketch, "E440", {"points": [v(-26.17, 31.6) * mm, v(-30.33, 30.53) * mm, v(-35.7, 28.07) * mm, v(-42.28, 24.22) * mm]});
            skFitSpline(sketch, "E441", {"points": [v(-12.89, 16.89) * mm, v(-12.52, 22.56) * mm, v(-12.33, 26.87) * mm, v(-12.33, 29.8) * mm]});
            skFitSpline(sketch, "E442", {"points": [v(-12.33, 29.8) * mm, v(-12.67, 29.8) * mm, v(-12.85, 30.1) * mm, v(-12.85, 30.7) * mm]});
            skFitSpline(sketch, "E443", {"points": [v(-12.85, 30.7) * mm, v(-13.62, 30.2) * mm, v(-16.23, 29.68) * mm, v(-20.68, 29.14) * mm]});
            skFitSpline(sketch, "E444", {"points": [v(-56.92, 4.92) * mm, v(-50.29, 7.28) * mm, v(-46.97, 8.83) * mm, v(-46.97, 9.56) * mm]});
            skFitSpline(sketch, "E445", {"points": [v(-46.42, 16.13) * mm, v(-54.03, 14.74) * mm, v(-57.83, 12.77) * mm, v(-57.83, 10.22) * mm]});
            skFitSpline(sketch, "E446", {"points": [v(-21.16, 7.33) * mm, v(-19.46, 7.33) * mm, v(-18.35, 7.13) * mm, v(-17.82, 6.72) * mm]});
            skFitSpline(sketch, "E447", {"points": [v(-13.84, 7.33) * mm, v(-13.84, 8.12) * mm, v(-13.67, 10.47) * mm, v(-13.32, 14.38) * mm]});
            skFitSpline(sketch, "E448", {"points": [v(-16.74, 13.62) * mm, v(-16.82, 13.62) * mm, v(-16.86, 13.9) * mm, v(-16.86, 14.43) * mm]});
            skFitSpline(sketch, "E449", {"points": [v(-16.86, 14.43) * mm, v(-19.73, 13.26) * mm, v(-21.16, 12.25) * mm, v(-21.16, 11.4) * mm]});
            skFitSpline(sketch, "E450", {"points": [v(-38.26, 7.95) * mm, v(-37.9, 3.97) * mm, v(-37.18, 1.99) * mm, v(-36.11, 1.99) * mm]});
            skFitSpline(sketch, "E451", {"points": [v(-33.8, 10.08) * mm, v(-35.8, 10.08) * mm, v(-37.28, 9.37) * mm, v(-38.26, 7.95) * mm]});
            skFitSpline(sketch, "E452", {"points": [v(-47.89, -23.75) * mm, v(-47.57, -23.75) * mm, v(-47.2, -24.22) * mm, v(-46.77, -25.17) * mm]});
            skFitSpline(sketch, "E453", {"points": [v(-46.77, -25.4) * mm, v(-49.27, -28.02) * mm, v(-50.94, -31.66) * mm, v(-51.79, -36.33) * mm]});
            skFitSpline(sketch, "E454", {"points": [v(-51.79, -36.33) * mm, v(-51.79, -36.87) * mm, v(-51.63, -37.51) * mm, v(-51.3, -38.27) * mm]});
            skFitSpline(sketch, "E455", {"points": [v(-51.3, -38.27) * mm, v(-51.3, -40.29) * mm, v(-52.6, -41.3) * mm, v(-55.17, -41.3) * mm]});
            skFitSpline(sketch, "E456", {"points": [v(-55.52, -38.79) * mm, v(-55.52, -34.82) * mm, v(-53.72, -29.96) * mm, v(-50.11, -24.22) * mm]});
            skFitSpline(sketch, "E457", {"points": [v(-21.92, -23.75) * mm, v(-17.73, -27.72) * mm, v(-15.63, -33.05) * mm, v(-15.63, -39.74) * mm]});
            skFitSpline(sketch, "E458", {"points": [v(-15.63, -39.74) * mm, v(-16.74, -40.78) * mm, v(-17.53, -41.3) * mm, v(-17.98, -41.3) * mm]});
            skFitSpline(sketch, "E459", {"points": [v(-17.98, -41.3) * mm, v(-19.78, -36.28) * mm, v(-21.76, -31.43) * mm, v(-23.9, -26.73) * mm]});
            skFitSpline(sketch, "E460", {"points": [v(-23.9, -26.73) * mm, v(-23.61, -24.74) * mm, v(-23.23, -23.75) * mm, v(-22.75, -23.75) * mm]});
            skFitSpline(sketch, "E461", {"points": [v(26.25, 38.7) * mm, v(28.42, 38.6) * mm, v(29.51, 38.24) * mm, v(29.51, 37.6) * mm]});
            skFitSpline(sketch, "E462", {"points": [v(29.51, 37.6) * mm, v(28.58, 35.78) * mm, v(27.81, 33.02) * mm, v(27.2, 29.33) * mm]});
            skFitSpline(sketch, "E463", {"points": [v(28.6, 29.33) * mm, v(32.9, 30.34) * mm, v(39.87, 32.9) * mm, v(49.52, 37.04) * mm]});
            skFitSpline(sketch, "E464", {"points": [v(49.52, 37.04) * mm, v(53.9, 38.14) * mm, v(56.7, 38.7) * mm, v(57.91, 38.7) * mm]});
            skFitSpline(sketch, "E465", {"points": [v(58.83, 38.7) * mm, v(63.12, 38.7) * mm, v(65.44, 37.04) * mm, v(65.79, 33.73) * mm]});
            skFitSpline(sketch, "E466", {"points": [v(65.79, 33.73) * mm, v(68.22, 33.73) * mm, v(70.1, 17.7) * mm, v(71.4, -14.38) * mm]});
            skFitSpline(sketch, "E467", {"points": [v(71.4, -16.6) * mm, v(71.4, -17.46) * mm, v(71.55, -18.2) * mm, v(71.87, -18.83) * mm]});
            skFitSpline(sketch, "E468", {"points": [v(71.87, -18.83) * mm, v(71.87, -28.67) * mm, v(70.32, -35.12) * mm, v(67.22, -38.17) * mm]});
            skFitSpline(sketch, "E469", {"points": [v(65.79, -38.17) * mm, v(63.93, -37.2) * mm, v(63, -36.47) * mm, v(63, -36) * mm]});
            skFitSpline(sketch, "E470", {"points": [v(63, -34.82) * mm, v(66.13, -34.82) * mm, v(67.7, -32.99) * mm, v(67.7, -29.33) * mm]});
            skFitSpline(sketch, "E471", {"points": [v(67.7, -29.33) * mm, v(68.17, -29.33) * mm, v(68.64, -25.83) * mm, v(69.09, -18.83) * mm]});
            skFitSpline(sketch, "E472", {"points": [v(69.09, -18.83) * mm, v(67.6, 14.35) * mm, v(65.43, 30.95) * mm, v(62.56, 30.98) * mm]});
            skFitSpline(sketch, "E473", {"points": [v(62.56, 30.98) * mm, v(62.03, 32.62) * mm, v(61.1, 33.93) * mm, v(59.78, 34.91) * mm]});
            skFitSpline(sketch, "E474", {"points": [v(56.96, 34.34) * mm, v(58.55, 34.28) * mm, v(59.95, 32.43) * mm, v(61.17, 28.8) * mm]});
            skFitSpline(sketch, "E475", {"points": [v(61.17, 28.8) * mm, v(57.96, 26.2) * mm, v(55.33, 24.88) * mm, v(53.26, 24.88) * mm]});
            skFitSpline(sketch, "E476", {"points": [v(53.26, 24.88) * mm, v(53.95, 14.92) * mm, v(54.73, 9.93) * mm, v(55.6, 9.93) * mm]});
            skFitSpline(sketch, "E477", {"points": [v(55.6, 9.93) * mm, v(56, 11.8) * mm, v(57.08, 12.72) * mm, v(58.83, 12.72) * mm]});
            skFitSpline(sketch, "E478", {"points": [v(58.83, 12.72) * mm, v(60.1, 12.16) * mm, v(60.73, 11.6) * mm, v(60.73, 11.07) * mm]});
            skFitSpline(sketch, "E479", {"points": [v(60.73, 11.07) * mm, v(60.73, 10.38) * mm, v(59.8, 9.43) * mm, v(57.91, 8.23) * mm]});
            skFitSpline(sketch, "E480", {"points": [v(57.91, 8.23) * mm, v(56.66, 5.05) * mm, v(56.04, 2.68) * mm, v(56.04, 1.14) * mm]});
            skFitSpline(sketch, "E481", {"points": [v(56.04, 1.14) * mm, v(58.3, -8.45) * mm, v(60.61, -16.02) * mm, v(63, -21.57) * mm]});
            skFitSpline(sketch, "E482", {"points": [v(63, -22.7) * mm, v(63, -24.91) * mm, v(62.07, -26.02) * mm, v(60.22, -26.02) * mm]});
            skFitSpline(sketch, "E483", {"points": [v(60.22, -26.02) * mm, v(56.21, -13.81) * mm, v(54.21, -6.26) * mm, v(54.21, -3.36) * mm]});
            skFitSpline(sketch, "E484", {"points": [v(49.52, -19.91) * mm, v(49.52, -22.5) * mm, v(48.29, -23.8) * mm, v(45.82, -23.8) * mm]});
            skFitSpline(sketch, "E485", {"points": [v(45.82, -23.8) * mm, v(45.82, -23.13) * mm, v(45.51, -22.22) * mm, v(44.9, -21.05) * mm]});
            skFitSpline(sketch, "E486", {"points": [v(44.9, -21.05) * mm, v(44.9, -18.69) * mm, v(47.38, -10.93) * mm, v(52.34, 2.22) * mm]});
            skFitSpline(sketch, "E487", {"points": [v(52.34, 3.31) * mm, v(52.34, 4.8) * mm, v(51.56, 11.43) * mm, v(50, 23.23) * mm]});
            skFitSpline(sketch, "E488", {"points": [v(50, 23.23) * mm, v(40.56, 18.05) * mm, v(35.13, 15.47) * mm, v(33.73, 15.47) * mm]});
            skFitSpline(sketch, "E489", {"points": [v(50, 32.6) * mm, v(49.39, 32.97) * mm, v(48.92, 33.16) * mm, v(48.6, 33.16) * mm]});
            skFitSpline(sketch, "E490", {"points": [v(48.6, 33.16) * mm, v(37.18, 27.64) * mm, v(29.9, 24.88) * mm, v(26.77, 24.88) * mm]});
            skFitSpline(sketch, "E491", {"points": [v(26.77, 24.88) * mm, v(23.98, 6.81) * mm, v(22.6, -3.33) * mm, v(22.6, -5.53) * mm]});
            skFitSpline(sketch, "E492", {"points": [v(22.6, -17.12) * mm, v(22.6, -17.82) * mm, v(23.35, -20.04) * mm, v(24.86, -23.8) * mm]});
            skFitSpline(sketch, "E493", {"points": [v(22.6, -28.24) * mm, v(20.4, -26.5) * mm, v(19.3, -23.2) * mm, v(19.3, -18.3) * mm]});
            skFitSpline(sketch, "E494", {"points": [v(19.3, -13.81) * mm, v(19.3, -5.55) * mm, v(21.46, 11.6) * mm, v(25.81, 37.65) * mm]});
            skFitSpline(sketch, "E495", {"points": [v(25.81, 37.65) * mm, v(26.1, 37.62) * mm, v(26.25, 37.97) * mm, v(26.25, 38.7) * mm]});
            skFitSpline(sketch, "E496", {"points": [v(52.34, 29.9) * mm, v(52.66, 28.04) * mm, v(52.97, 27.1) * mm, v(53.26, 27.1) * mm]});
            skFitSpline(sketch, "E497", {"points": [v(53.26, 27.1) * mm, v(54.82, 28.2) * mm, v(55.9, 28.76) * mm, v(56.52, 28.76) * mm]});
            skFitSpline(sketch, "E498", {"points": [v(56.52, 28.76) * mm, v(54.98, 30.78) * mm, v(54.21, 31.88) * mm, v(54.21, 32.07) * mm]});
            skFitSpline(sketch, "E499", {"points": [v(54.65, 34.86) * mm, v(54.12, 34.45) * mm, v(53.5, 34.25) * mm, v(52.82, 34.25) * mm]});
            skFitSpline(sketch, "E500", {"points": [v(33.25, 14.9) * mm, v(33.6, 14.9) * mm, v(34.36, 13.8) * mm, v(35.56, 11.59) * mm]});
            skFitSpline(sketch, "E501", {"points": [v(35.56, 11.59) * mm, v(37.63, 12.7) * mm, v(39.8, 13.25) * mm, v(42.08, 13.25) * mm]});
            skFitSpline(sketch, "E502", {"points": [v(43.47, 11.07) * mm, v(43.18, 8.83) * mm, v(42.72, 7.71) * mm, v(42.08, 7.71) * mm]});
            skFitSpline(sketch, "E503", {"points": [v(42.52, 6.58) * mm, v(42.52, 5.88) * mm, v(42.07, 5.53) * mm, v(41.17, 5.53) * mm]});
            skFitSpline(sketch, "E504", {"points": [v(41.64, 1.66) * mm, v(37.8, -1.69) * mm, v(35.46, -3.36) * mm, v(34.64, -3.36) * mm]});
            skFitSpline(sketch, "E505", {"points": [v(34.17, -3.36) * mm, v(33.18, -3.36) * mm, v(32.27, 0.91) * mm, v(31.42, 9.46) * mm]});
            skFitSpline(sketch, "E506", {"points": [v(31.42, 13.86) * mm, v(31.5, 14.55) * mm, v(31.8, 14.9) * mm, v(32.34, 14.9) * mm]});
            skFitSpline(sketch, "E507", {"points": [v(36.03, 3.88) * mm, v(36.27, 3.88) * mm, v(37.21, 5.33) * mm, v(38.86, 8.23) * mm]});
            skFitSpline(sketch, "E508", {"points": [v(38.38, 8.23) * mm, v(37.19, 7.13) * mm, v(36.25, 6.58) * mm, v(35.56, 6.58) * mm]});
            skFitSpline(sketch, "E509", {"points": [v(45.82, -5.01) * mm, v(45.6, -6.46) * mm, v(40.34, -9.57) * mm, v(30.03, -14.33) * mm]});
            skFitSpline(sketch, "E510", {"points": [v(29.51, -14.38) * mm, v(28.9, -14.35) * mm, v(28.6, -13.97) * mm, v(28.6, -13.25) * mm]});
            skFitSpline(sketch, "E511", {"points": [v(28.6, -13.25) * mm, v(28.6, -10.88) * mm, v(30.45, -9.22) * mm, v(34.17, -8.28) * mm]});
            skFitSpline(sketch, "E512", {"points": [v(34.17, -8.28) * mm, v(35.2, -7.17) * mm, v(38.93, -5.7) * mm, v(45.34, -3.88) * mm]});
            skFitSpline(sketch, "E513", {"points": [v(54.65, -29.33) * mm, v(54.65, -31.06) * mm, v(49.39, -32.17) * mm, v(38.86, -32.64) * mm]});
            skFitSpline(sketch, "E514", {"points": [v(32.77, -32.64) * mm, v(32.32, -32.6) * mm, v(31.87, -32.04) * mm, v(31.42, -30.94) * mm]});
            skFitSpline(sketch, "E515", {"points": [v(32.34, -28.8) * mm, v(35.07, -29.15) * mm, v(36.78, -29.33) * mm, v(37.47, -29.33) * mm]});
            skFitSpline(sketch, "E516", {"points": [v(37.47, -29.33) * mm, v(38.18, -29.33) * mm, v(40.52, -29.15) * mm, v(44.47, -28.8) * mm]});
            skFitSpline(sketch, "E517", {"points": [v(45.34, -29.33) * mm, v(45.87, -29.04) * mm, v(47.73, -28.68) * mm, v(50.91, -28.24) * mm]});
            skFitSpline(sketch, "E518", {"points": [v(136.07, 43.61) * mm, v(136.52, 37.65) * mm, v(136.74, 33.32) * mm, v(136.74, 30.6) * mm]});
            skFitSpline(sketch, "E519", {"points": [v(147.68, 26.77) * mm, v(150.07, 26.77) * mm, v(151.79, 25.5) * mm, v(152.85, 22.94) * mm]});
            skFitSpline(sketch, "E520", {"points": [v(152.85, 22.94) * mm, v(152.85, 18.69) * mm, v(149.2, 14.82) * mm, v(141.87, 11.35) * mm]});
            skFitSpline(sketch, "E521", {"points": [v(142.55, 10.64) * mm, v(144.9, 11.12) * mm, v(146.62, 11.38) * mm, v(147.68, 11.45) * mm]});
            skFitSpline(sketch, "E522", {"points": [v(147.68, 11.45) * mm, v(149.4, 10.63) * mm, v(150.26, 9.84) * mm, v(150.26, 9.08) * mm]});
            skFitSpline(sketch, "E523", {"points": [v(150.26, 8.33) * mm, v(150.26, 7.32) * mm, v(149.84, 6.81) * mm, v(149, 6.81) * mm]});
            skFitSpline(sketch, "E524", {"points": [v(149, 6.81) * mm, v(140.82, 6.81) * mm, v(136.74, 6.04) * mm, v(136.74, 4.5) * mm]});
            skFitSpline(sketch, "E525", {"points": [v(136.74, 4.5) * mm, v(136.74, -3.67) * mm, v(136.52, -17.25) * mm, v(136.07, -36.23) * mm]});
            skFitSpline(sketch, "E526", {"points": [v(132.88, -43.14) * mm, v(132, -43.14) * mm, v(131.57, -42.64) * mm, v(131.57, -41.63) * mm]});
            skFitSpline(sketch, "E527", {"points": [v(131.57, -40.87) * mm, v(131.57, -24.98) * mm, v(132, -9.85) * mm, v(132.88, 4.5) * mm]});
            skFitSpline(sketch, "E528", {"points": [v(130.3, 4.5) * mm, v(128.02, 4.5) * mm, v(124.33, 4.24) * mm, v(119.24, 3.74) * mm]});
            skFitSpline(sketch, "E529", {"points": [v(119.24, 5.25) * mm, v(119.24, 6.3) * mm, v(123.56, 7.32) * mm, v(132.2, 8.33) * mm]});
            skFitSpline(sketch, "E530", {"points": [v(132.88, 10.64) * mm, v(132.88, 13.36) * mm, v(133.08, 17.7) * mm, v(133.48, 23.7) * mm]});
            skFitSpline(sketch, "E531", {"points": [v(132.88, 23.7) * mm, v(127.63, 23.7) * mm, v(120.29, 21.9) * mm, v(110.85, 18.3) * mm]});
            skFitSpline(sketch, "E532", {"points": [v(110.85, 18.3) * mm, v(110.45, 10.64) * mm, v(110.25, 5.01) * mm, v(110.25, 1.42) * mm]});
            skFitSpline(sketch, "E533", {"points": [v(110.25, -1.66) * mm, v(110.25, -4.37) * mm, v(110.89, -8.47) * mm, v(112.16, -13.95) * mm]});
            skFitSpline(sketch, "E534", {"points": [v(108.94, -15.47) * mm, v(107.06, -15.47) * mm, v(105.77, -10.88) * mm, v(105.08, -1.7) * mm]});
            skFitSpline(sketch, "E535", {"points": [v(105.08, -1.7) * mm, v(105.93, 15.48) * mm, v(107.22, 28.05) * mm, v(108.94, 36) * mm]});
            skFitSpline(sketch, "E536", {"points": [v(110.85, 19.87) * mm, v(119.36, 23.97) * mm, v(126.9, 26.02) * mm, v(133.48, 26.02) * mm]});
            skFitSpline(sketch, "E537", {"points": [v(133.48, 26.77) * mm, v(133.9, 32.36) * mm, v(134.12, 37.21) * mm, v(134.12, 41.34) * mm]});
            skFitSpline(sketch, "E538", {"points": [v(136.74, 10.64) * mm, v(144.56, 15.09) * mm, v(149.07, 18.67) * mm, v(150.26, 21.38) * mm]});
            skFitSpline(sketch, "E539", {"points": [v(150.26, 22.94) * mm, v(150.26, 23.98) * mm, v(149.84, 24.5) * mm, v(149, 24.5) * mm]});
            skSolve(sketch);
        }
        {
            var Q0;
            Q0=makeQuery(id+"F0.imprint","IMPRINT",FACE,{"disambiguationData":[TD([[makeQuery(id+"F0.imprint","IMPRINT",EDGE,{"derivedFrom":sQuery(id+"F0.wireOp",EDGE,"E1")}),1.0]])]});
            var Q1;
            Q1=makeQuery(id+"F0.imprint","IMPRINT",FACE,{"disambiguationData":[TD([[makeQuery(id+"F0.imprint","IMPRINT",EDGE,{"derivedFrom":sQuery(id+"F0.wireOp",EDGE,"E23")}),1.0]])]});
            var Q2;
            Q2=makeQuery(id+"F0.imprint","IMPRINT",FACE,{"disambiguationData":[TD([[makeQuery(id+"F0.imprint","IMPRINT",EDGE,{"derivedFrom":sQuery(id+"F0.wireOp",EDGE,"E95")}),1.0]])]});
            var Q3;
            Q3=makeQuery(id+"F0.imprint","IMPRINT",FACE,{"disambiguationData":[TD([[makeQuery(id+"F0.imprint","IMPRINT",EDGE,{"derivedFrom":sQuery(id+"F0.wireOp",EDGE,"E191")}),1.0]])]});
            var Q4;
            Q4=makeQuery(id+"F0.imprint","IMPRINT",FACE,{"disambiguationData":[TD([[makeQuery(id+"F0.imprint","IMPRINT",EDGE,{"derivedFrom":sQuery(id+"F0.wireOp",EDGE,"E200")}),1.0]])]});
            var Q5;
            Q5=makeQuery(id+"F0.imprint","IMPRINT",FACE,{"disambiguationData":[TD([[makeQuery(id+"F0.imprint","IMPRINT",EDGE,{"derivedFrom":sQuery(id+"F0.wireOp",EDGE,"E202")}),1.0]])]});
            var Q6;
            Q6=makeQuery(id+"F0.imprint","IMPRINT",FACE,{"disambiguationData":[TD([[makeQuery(id+"F0.imprint","IMPRINT",EDGE,{"derivedFrom":sQuery(id+"F0.wireOp",EDGE,"E245")}),1.0]])]});
            var Q7;
            Q7=makeQuery(id+"F0.imprint","IMPRINT",FACE,{"disambiguationData":[TD([[makeQuery(id+"F0.imprint","IMPRINT",EDGE,{"derivedFrom":sQuery(id+"F0.wireOp",EDGE,"E263")}),1.0]])]});
            var Q8;
            {var subQ4=sQuery(id+"F0.wireOp",EDGE,"E267");Q8=makeQuery(id+"F0.imprint","IMPRINT",FACE,{"disambiguationData":[TD([[makeQuery(id+"F0.imprint","IMPRINT",EDGE,{"derivedFrom":subQ4}),-1.0]])]});}
            var Q9;
            Q9=makeQuery(id+"F0.imprint","IMPRINT",FACE,{"disambiguationData":[TD([[makeQuery(id+"F0.imprint","IMPRINT",EDGE,{"derivedFrom":sQuery(id+"F0.wireOp",EDGE,"E280")}),1.0]])]});
            extrude(context, id + "F1", {"entities" : qUnion([Q0, Q1, Q2, Q3, Q4, Q5, Q6, Q7, Q8, Q9]), "depth" : 1 * mm, "offsetDistance" : 25 * mm});
        }
    });
